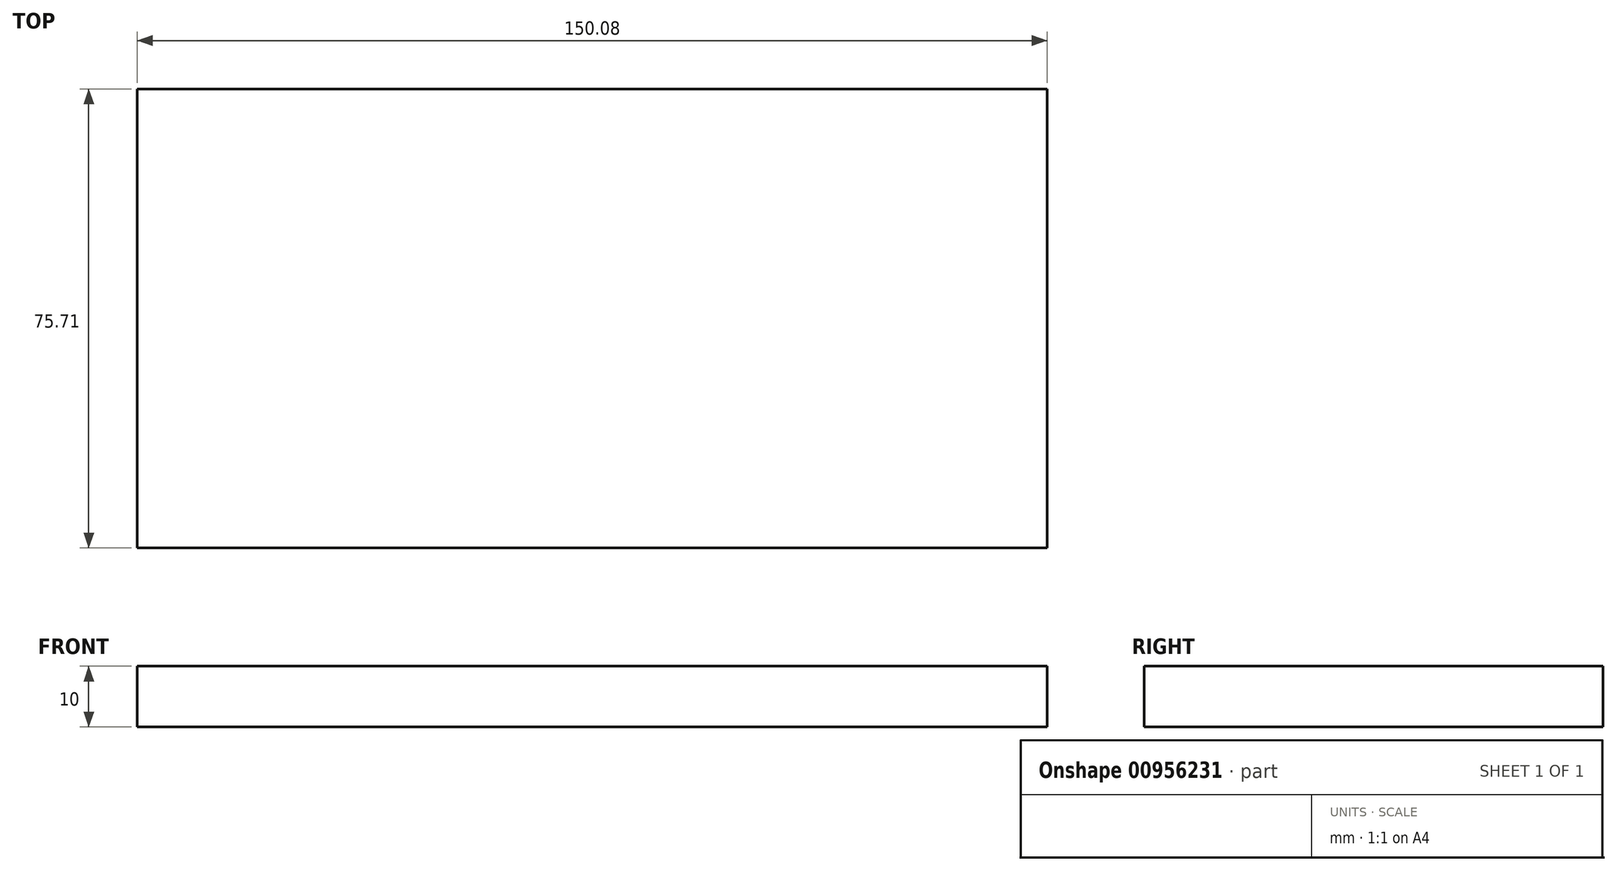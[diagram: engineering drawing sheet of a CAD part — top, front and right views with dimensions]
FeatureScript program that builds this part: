
annotation { "Feature Type Name" : "Feature", "Feature Type Description" : "" }
export const myFeature = defineFeature(function(context is Context, id is Id, definition is map)
    precondition{}
    {
        {
            var Q0;
            Q0=qCreatedBy(makeId("Top.planeOp"),FACE);
            var sketch = newSketch(context, id + "F0", { "sketchPlane" : qUnion([Q0])});
            skLineSegment(sketch, "E0.bottom", {"start": v(-129.37, 29.23) * mm, "end": v(20.71, 29.23) * mm});
            skLineSegment(sketch, "E0.top", {"start": v(-129.37, -46.48) * mm, "end": v(20.71, -46.48) * mm});
            skLineSegment(sketch, "E0.left", {"start": v(-129.37, 29.23) * mm, "end": v(-129.37, -46.48) * mm});
            skLineSegment(sketch, "E0.right", {"start": v(20.71, 29.23) * mm, "end": v(20.71, -46.48) * mm});
            skSolve(sketch);
        }
        {
            var Q0;
            Q0=makeQuery(id+"F0.imprint","IMPRINT",FACE,{"disambiguationData":[TD([[makeQuery(id+"F0.imprint","IMPRINT",EDGE,{"derivedFrom":sQuery(id+"F0.wireOp",EDGE,"E0.bottom")}),-1.0]])]});
            extrude(context, id + "F1", {"entities" : qUnion([Q0]), "depth" : 10 * mm, "offsetDistance" : 25.4 * mm});
        }
    });
